# Revit family: PRD_AR_TltRllHldrs_DoubleToiletRollHolder_CHRX676N
name_source: partatom
category: Specialty Equipment
revit_build: Autodesk Revit 2018 (Build: 20190510_1515(x64)
units: mm (PartAtom-declared; Revit-internal decimal feet)

## family parameters
Cut with Voids When Loaded = No
Host = Face
OmniClass Number = 23.40.20.21.21
OmniClass Title = Toilet Paper Dispensers
Part Type = Normal
Room Calculation Point = No
Round Connector Dimension = Use Diameter
Shared = No

## types (1)
- CHRX676N
    AssetType = Fixed
    BIMObjectName = PRD_AR_ToiletRollHolders_DoubleToiletRollHolder_CHRX676N
    Category = Pr_40_20_76_88, Toilet roll holders
    Default Elevation = 700 mm  [stored 2.29659 ft]
    Description = Double toilet roll holder for wall mounting, stainless steel, surface satin finished, material thickness 2 mm, cylinder lock with KWC standard key, for 2 rolls with a maximum diameter of 140 mm, thief protected spindles, controlled paper consumption due to spindle stop mechanism, includes stainless steel screws and dowels.
    DurationUnit = year
    Features = stainless steel, included fixing material
    FillingQuantity = 2
    FillingQuantityUom = Rolls
    Finish = satin finished
    GrossWeight = 1.50 kg
    IfcExportAs = IfcFurnitureType
    IfcExportType = USERDEFINED
    IntegralAccessories = incl. stainless steel screws and dowels
    IsBuiltIn = TRUE
    Lock = Key-lock
    MainColor = stainless steel
    Manufacturer = KWC Group AG
    ManufacturerName = KWC Group AG
    ManufacturerURL = www.kwc.com
    Material = stainless steel
    MaterialCode = 1.4301
    MaterialThickness = 2.00 mm
    MaximumDepthDiameterOfConsumable = 140.00 mm
    MaximumWidthOfConsumable = 140.00 mm
    Model = CHRX676N
    ModelNumber = 2030028851
    ModelReference = CHRX676N
    NBSDescription = Toilet roll holders
    NBSReference = 45-35-72/368
    Name = Double toilet roll holder CHRX676N
    NetWeight = 1.42 kg
    NominalDepth = 132 mm  [stored 0.433071 ft]
    NominalHeight = 98 mm  [stored 0.321522 ft]
    NominalWidth = 335 mm  [stored 1.09908 ft]
    ProductInformation = https://pim.kwc.com
    RollHolderMaterial = PRD_AR_StainlessSteel_SatinFinished
    Size = 335 x 98 x 132 mm
    Spindle = Yes
    Style = Toilet roll holder
    ToiletRollMaterial = PRD_AR_ToiletRoll
    TypeOfFixing = Screw
    TypeOfMounting = Wall mounting
    URL = www.kwc.com
    Uniclass2015Code = Pr_40_20_76_88
    Uniclass2015Title = Toilet roll holders
    Uniclass2015Version = Products v1.10
    Version = 1
    WarrantyDurationUnit = year

note: [stored X ft] marks values corroborated as IEEE doubles in the binary element streams (Revit-internal decimal feet)

## geometry (parser evidence)
native form markers: Sweep x2
no freeform markers — native parametric forms only
